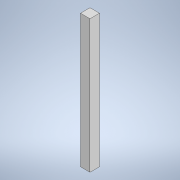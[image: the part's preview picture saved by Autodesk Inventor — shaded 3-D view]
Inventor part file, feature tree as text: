
AUTODESK INVENTOR PART (.ipt)
format: ipt  version: 2021 (Build 250183000, 183)  size: 93,184 bytes
history: native  units: mm
features: extrude x1, sketch x1
ambient origin geometry x8: Origin, YZ Plane, XZ Plane, XY Plane, X Axis, Y Axis, Z Axis, Center Point
bodies: Solid1 (feature_tree)
feature tree (2):
  extrude  "Extrusion1"  Depth=100.0mm
  sketch  "Sketch1"  dims[d0=100.0mm d1=100.0mm d2=1400.0mm d3=0.0mm]
